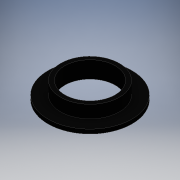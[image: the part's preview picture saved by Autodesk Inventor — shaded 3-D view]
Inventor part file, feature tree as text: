
AUTODESK INVENTOR PART (.ipt)
format: ipt  version: 2020.2 (Build 242310000, 310)  size: 104,448 bytes
history: native  units: mm
features: extrude x2, other x1, sketch x1
ambient origin geometry x8: Origin, YZ Plane, XZ Plane, XY Plane, X Axis, Y Axis, Z Axis, Center Point
bodies: Body1 (feature_tree)
feature tree (4):
  other  "ソリッド1"
  sketch  "スケッチ1"
  extrude  "押し出し1"  Depth=12.0mm
  extrude  "押し出し2"  Depth=14.0mm
